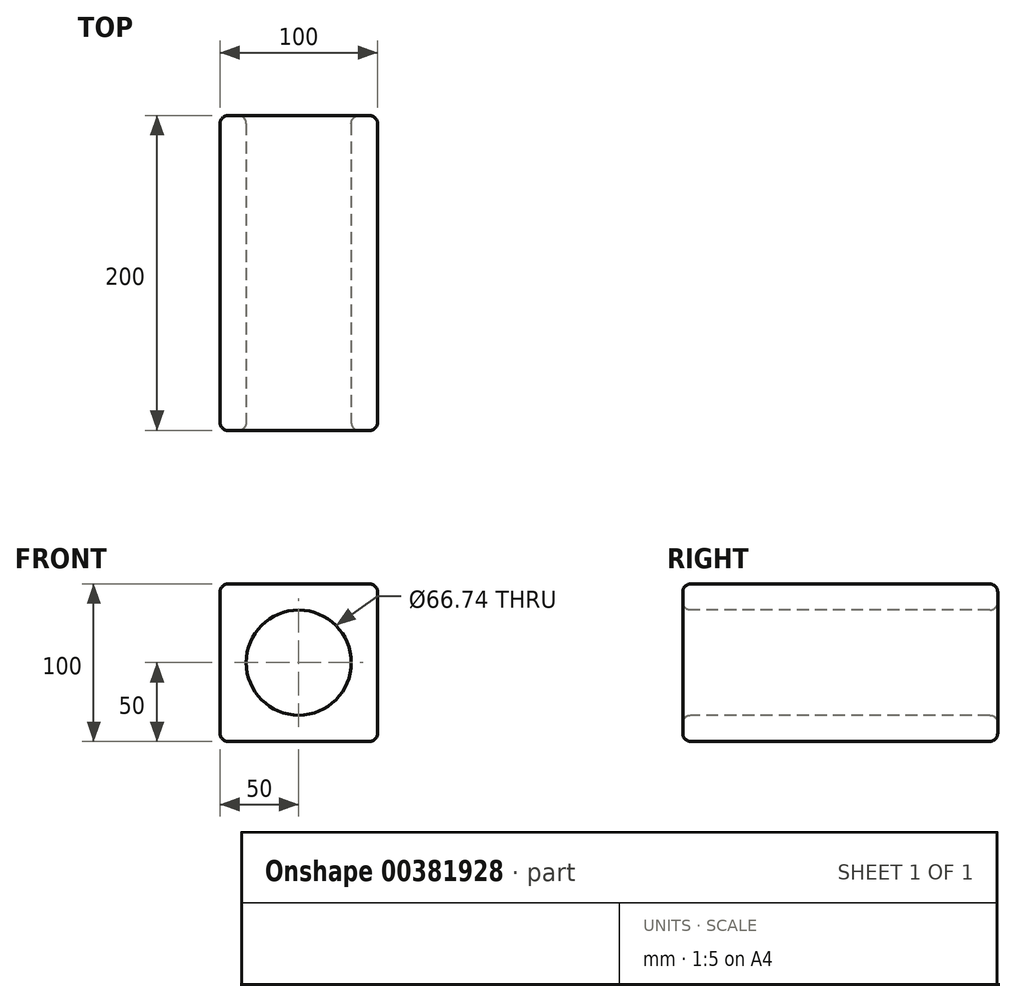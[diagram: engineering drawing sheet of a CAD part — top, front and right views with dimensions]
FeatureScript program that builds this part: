
annotation { "Feature Type Name" : "Feature", "Feature Type Description" : "" }
export const myFeature = defineFeature(function(context is Context, id is Id, definition is map)
    precondition{}
    {
        {
            var Q0;
            Q0=qCreatedBy(makeId("Front.planeOp"),FACE);
            var sketch = newSketch(context, id + "F0", { "sketchPlane" : qUnion([Q0])});
            skLineSegment(sketch, "E0.bottom", {"start": v(50, 50) * mm, "end": v(-50, 50) * mm});
            skLineSegment(sketch, "E0.top", {"start": v(50, -50) * mm, "end": v(-50, -50) * mm});
            skLineSegment(sketch, "E0.left", {"start": v(50, 50) * mm, "end": v(50, -50) * mm});
            skLineSegment(sketch, "E0.right", {"start": v(-50, 50) * mm, "end": v(-50, -50) * mm});
            skPoint(sketch, "E0.middle", {"position": v(0, 0) * mm});
            skSolve(sketch);
        }
        {
            var Q0;
            Q0 = qSketchRegion(id + "F0", true);
            extrude(context, id + "F1", {"entities" : qUnion([Q0]), "depth" : 200 * mm});
        }
        {
            var Q0;
            Q0=makeQuery(id+"F1.opExtrude","CAP_FACE",FACE,{"disambiguationData":[OSD([sQuery(id+"F0.wireOp",EDGE,"E0.bottom"),sQuery(id+"F0.wireOp",EDGE,"E0.top"),sQuery(id+"F0.wireOp",EDGE,"E0.left"),sQuery(id+"F0.wireOp",EDGE,"E0.right")])],"isStart":false});
            var sketch = newSketch(context, id + "F2", { "sketchPlane" : qUnion([Q0])});
            skCircle(sketch, "E1", {"center": v(0, 0) * mm, "radius": 33.37 * mm});
            skSolve(sketch);
        }
        {
            var Q0;
            Q0 = qSketchRegion(id + "F2", true);
            extrude(context, id + "F3", {"entities" : qUnion([Q0]), "operationType" : NewBodyOperationType.REMOVE, "oppositeDirection" : true, "depth" : 273 * mm});
        }
        {
            var Q0;
            Q0=makeQuery(id+"F1.opExtrude","SWEPT_FACE",FACE,{"disambiguationData":[OSD([sQuery(id+"F0.wireOp",EDGE,"E0.bottom")])]});
            var Q1;
            Q1=makeQuery(id+"F1.opExtrude","SWEPT_FACE",FACE,{"disambiguationData":[OSD([sQuery(id+"F0.wireOp",EDGE,"E0.right")])]});
            var Q2;
            Q2=makeQuery(id+"F1.opExtrude","CAP_FACE",FACE,{"disambiguationData":[OSD([sQuery(id+"F0.wireOp",EDGE,"E0.bottom"),sQuery(id+"F0.wireOp",EDGE,"E0.top"),sQuery(id+"F0.wireOp",EDGE,"E0.left"),sQuery(id+"F0.wireOp",EDGE,"E0.right")])],"isStart":true});
            var Q3;
            Q3=makeQuery(id+"F1.opExtrude","SWEPT_FACE",FACE,{"disambiguationData":[OSD([sQuery(id+"F0.wireOp",EDGE,"E0.left")])]});
            var Q4;
            Q4=makeQuery(id+"F1.opExtrude","SWEPT_FACE",FACE,{"disambiguationData":[OSD([sQuery(id+"F0.wireOp",EDGE,"E0.top")])]});
            var Q5;
            Q5=makeQuery(id+"F1.opExtrude","CAP_FACE",FACE,{"disambiguationData":[OSD([sQuery(id+"F0.wireOp",EDGE,"E0.bottom"),sQuery(id+"F0.wireOp",EDGE,"E0.top"),sQuery(id+"F0.wireOp",EDGE,"E0.left"),sQuery(id+"F0.wireOp",EDGE,"E0.right")])],"isStart":false});
            fillet(context, id + "F4", {"entities" : qUnion([Q0, Q1, Q2, Q3, Q4, Q5]), "radius" : 5 * mm, "tangentPropagation" : true, "allowEdgeOverflow" : false});
        }
    });
